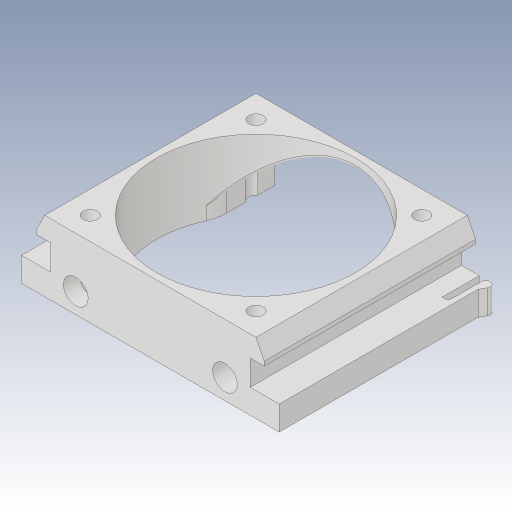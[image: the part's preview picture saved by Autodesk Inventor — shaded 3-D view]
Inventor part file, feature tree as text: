
AUTODESK INVENTOR PART (.ipt)
format: ipt  version: 2023.3 (Build 273359000, 359)  size: 297,472 bytes
history: native  units: in
note: dims shown in document units (in); Inventor stores cm internally (conversion verified against a paired STEP export)
features: extrude x6, sketch x6, fillet x3, plane x2, chamfer x2, hole x1, mirror x1, projected_geometry x1
ambient origin geometry x8: Origin, YZ Plane, XZ Plane, XY Plane, X Axis, Y Axis, Z Axis, Center Point
bodies: Body1 (feature_tree)
feature tree (22):
  extrude  "Extrusion3"  Depth=0.1211in
  plane  "Arbeitsebene1"
  extrude  "Extrusion4"  Depth=0.1378in
  chamfer  "Fase1"  Distance=1.0039in
  extrude  "Extrusion5"  Depth=0.8268in TaperAngle=0.0deg
  fillet  "Rundung1"  Radius=0.962in
  fillet  "Rundung2"  Radius=1.0827in
  hole  "Bohrung1"  [1 undecoded]
  sketch  "Skizze7"  dims[d20=0.9449in d21=0.502in]
  extrude  "Extrusion6"  Depth=0.502in
  extrude  "Extrusion7"  Depth=0.3937in
  fillet  "Rundung3"  Radius=0.0157in
  plane  "Arbeitsebene2"
  mirror  "Spiegeln1"
  chamfer  "Fase3"  Distance=0.7874in
  extrude  "Extrusion8"  Depth=0.3937in
  sketch  "Skizze3"  dims[d4=0.9488in d5=0.1211in]
  sketch  "Skizze4"  dims[d6=0.1152in d7=0.1378in d8=1.0039in d9=0.0in]
  sketch  "Skizze5"  dims[d10=0.2953in d12=0.8268in d13=0.0in d14=0.962in d15=1.0827in]
  sketch  "Skizze6"  dims[d16=0.0984in d17=0.0394in d18=0.0787in d19=45.0deg]
  projected_geometry  "Projizierte Kontur1"
  sketch  "Skizze8"  dims[d22=0.7874in d23=0.0in d27=0.1969in d28=0.0157in d29=0.7874in d30=0.0689in d31=0.1969in d32=0.119in d33=0.0787in d34=0.5635in d35=0.248in d36=0.0in d38=0.0531in d39=0.0236in d40=0.0394in d41=0.1772in d42=0.1181in d43=0.0in d44=0.1181in d45=0.0in d46=0.0157in d47=0.0197in d48=0.0787in d49=45.0deg d50=0.1181in d51=0.1181in d52=0.0197in d53=0.7087in d54=0.3543in d55=0.3937in d56=0.0in]
note: 1 required parameter value undecoded (feature->parameter linkage not recoverable at this tier; creation-order binding heuristic only, values carry confidence <= 0.55)
